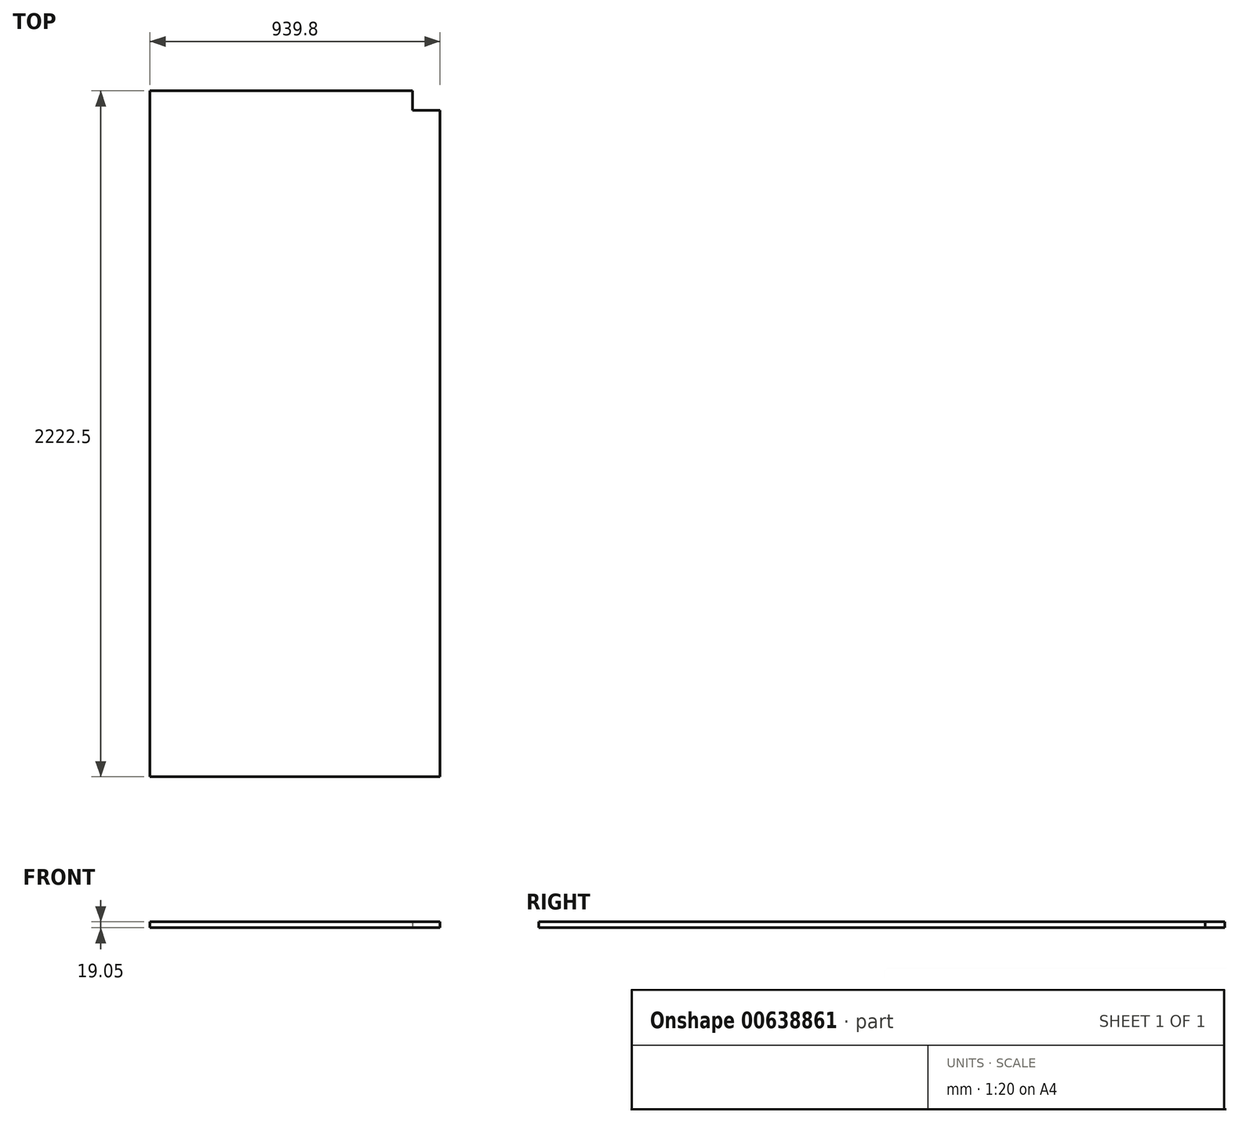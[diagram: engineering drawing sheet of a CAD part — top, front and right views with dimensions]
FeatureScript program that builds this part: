
annotation { "Feature Type Name" : "Feature", "Feature Type Description" : "" }
export const myFeature = defineFeature(function(context is Context, id is Id, definition is map)
    precondition{}
    {
        {
            var Q0;
            Q0=qCreatedBy(makeId("Top.planeOp"),FACE);
            var sketch = newSketch(context, id + "F0", { "sketchPlane" : qUnion([Q0])});
            skLineSegment(sketch, "E0.bottom", {"start": v(0, 0) * mm, "end": v(939.8, 0) * mm});
            skLineSegment(sketch, "E0.top", {"start": v(0, 2222.5) * mm, "end": v(939.8, 2222.5) * mm});
            skLineSegment(sketch, "E0.left", {"start": v(0, 0) * mm, "end": v(0, 2222.5) * mm});
            skLineSegment(sketch, "E0.right", {"start": v(939.8, 0) * mm, "end": v(939.8, 2222.5) * mm});
            skLineSegment(sketch, "E1.bottom", {"start": v(939.8, 2222.5) * mm, "end": v(850.9, 2222.5) * mm});
            skLineSegment(sketch, "E1.top", {"start": v(939.8, 2159) * mm, "end": v(850.9, 2159) * mm});
            skLineSegment(sketch, "E1.left", {"start": v(939.8, 2222.5) * mm, "end": v(939.8, 2159) * mm});
            skLineSegment(sketch, "E1.right", {"start": v(850.9, 2222.5) * mm, "end": v(850.9, 2159) * mm});
            skSolve(sketch);
        }
        {
            var Q0;
            Q0=makeQuery(id+"F0.imprint","IMPRINT",FACE,{"disambiguationData":[TD([[makeQuery(id+"F0.imprint","IMPRINT",EDGE,{"derivedFrom":sQuery(id+"F0.wireOp",EDGE,"E0.bottom")}),1.0]])]});
            extrude(context, id + "F1", {"entities" : qUnion([Q0]), "depth" : 19.05 * mm, "offsetDistance" : 25.4 * mm});
        }
    });
